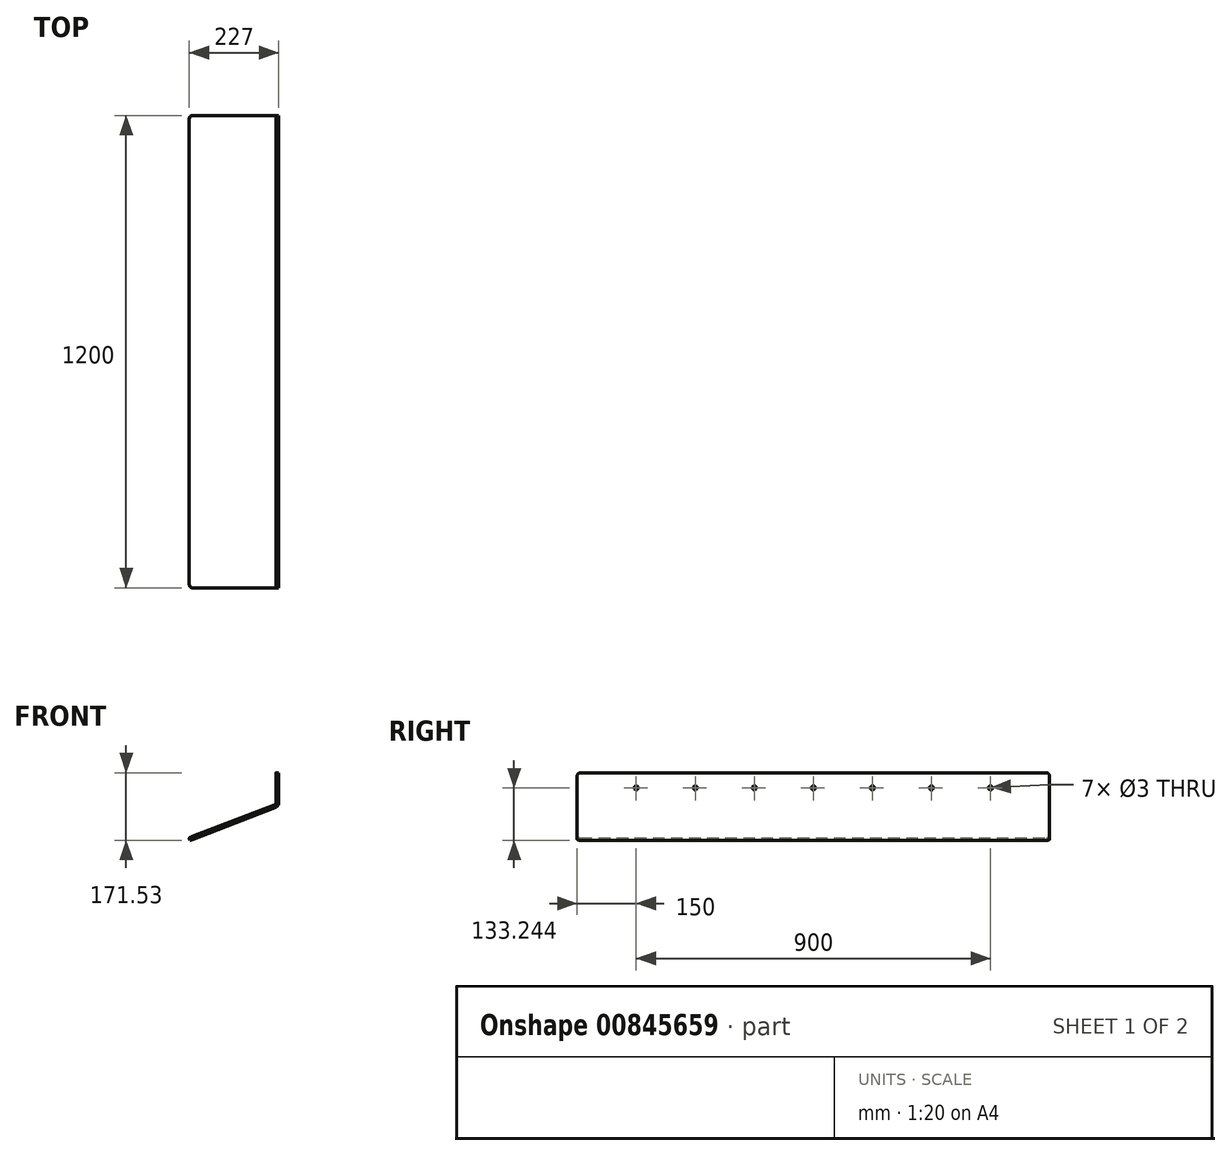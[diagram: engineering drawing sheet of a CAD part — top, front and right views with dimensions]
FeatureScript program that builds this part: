
annotation { "Feature Type Name" : "Feature", "Feature Type Description" : "" }
export const myFeature = defineFeature(function(context is Context, id is Id, definition is map)
    precondition{}
    {
        {
            var Q0;
            Q0=qCreatedBy(makeId("Front.planeOp"),FACE);
            var sketch = newSketch(context, id + "F0", { "sketchPlane" : qUnion([Q0])});
            skLineSegment(sketch, "E0", {"start": v(0, 80) * mm, "end": v(0, 3.43) * mm});
            skLineSegment(sketch, "E1", {"start": v(-3.2, -1.24) * mm, "end": v(-220, -85) * mm});
            skLineSegment(sketch, "E2", {"start": v(-220, -85) * mm, "end": v(-217.48, -91.53) * mm});
            skLineSegment(sketch, "E3", {"start": v(-217.48, -91.53) * mm, "end": v(-0.68, -7.77) * mm});
            skLineSegment(sketch, "E4", {"start": v(7, 3.43) * mm, "end": v(7, 80) * mm});
            skLineSegment(sketch, "E5", {"start": v(7, 80) * mm, "end": v(0, 80) * mm});
            skPoint(sketch, "E6.visualSharp", {"position": v(0, 0) * mm});
            skArc(sketch, "E6.filletArc", {"start": v(-3.2, -1.24) * mm, "mid": v(-0.88, 0.6) * mm, "end": v(0, 3.43) * mm});
            skPoint(sketch, "E7.visualSharp", {"position": v(7, -4.8) * mm});
            skArc(sketch, "E7.filletArc", {"start": v(-0.68, -7.77) * mm, "mid": v(4.9, -3.36) * mm, "end": v(7, 3.43) * mm});
            skSolve(sketch);
        }
        {
            var Q0;
            Q0=makeQuery(id+"F0.imprint","IMPRINT",FACE,{"disambiguationData":[TD([[makeQuery(id+"F0.imprint","IMPRINT",EDGE,{"derivedFrom":sQuery(id+"F0.wireOp",EDGE,"E0")}),1.0]])]});
            extrude(context, id + "F1", {"entities" : qUnion([Q0]), "depth" : 1200 * mm, "offsetDistance" : 25 * mm});
        }
        {
            var Q0;
            Q0=makeQuery(id+"F1.opExtrude","CAP_EDGE",EDGE,{"disambiguationData":[OSD([sQuery(id+"F0.wireOp",EDGE,"E5")])],"isStart":false});
            var Q1;
            Q1=makeQuery(id+"F1.opExtrude","CAP_EDGE",EDGE,{"disambiguationData":[OSD([sQuery(id+"F0.wireOp",EDGE,"E5")])],"isStart":true});
            var Q2;
            Q2=makeQuery(id+"F1.opExtrude","CAP_EDGE",EDGE,{"disambiguationData":[OSD([sQuery(id+"F0.wireOp",EDGE,"E2")])],"isStart":true});
            var Q3;
            Q3=makeQuery(id+"F1.opExtrude","CAP_EDGE",EDGE,{"disambiguationData":[OSD([sQuery(id+"F0.wireOp",EDGE,"E2")])],"isStart":false});
            fillet(context, id + "F2", {"entities" : qUnion([Q0, Q1, Q2, Q3]), "radius" : 8 * mm, "tangentPropagation" : true, "allowEdgeOverflow" : false});
        }
        {
            var Q0;
            Q0=makeQuery(id+"F1.opExtrude","SWEPT_FACE",FACE,{"disambiguationData":[OSD([sQuery(id+"F0.wireOp",EDGE,"E4")])]});
            var sketch = newSketch(context, id + "F3", { "sketchPlane" : qUnion([Q0])});
            skLineSegment(sketch, "E8", {"start": v(-1288.33, 41.71) * mm, "end": v(83.25, 41.71) * mm, "construction": true});
            skPoint(sketch, "E9", {"position": v(-1050, 41.71) * mm});
            skPoint(sketch, "E10", {"position": v(-900, 41.71) * mm});
            skPoint(sketch, "E11", {"position": v(-750, 41.71) * mm});
            skPoint(sketch, "E12", {"position": v(-600, 41.71) * mm});
            skPoint(sketch, "E13", {"position": v(-450, 41.71) * mm});
            skPoint(sketch, "E14", {"position": v(-300, 41.71) * mm});
            skPoint(sketch, "E15", {"position": v(-150, 41.71) * mm});
            skSolve(sketch);
        }
        {
            var Q0;
            Q0=sQuery(id+"F3.wireOp",VERTEX,"E10");
            var Q1;
            Q1=sQuery(id+"F3.wireOp",VERTEX,"E9");
            var Q2;
            Q2=sQuery(id+"F3.wireOp",VERTEX,"E11");
            var Q3;
            Q3=sQuery(id+"F3.wireOp",VERTEX,"E12");
            var Q4;
            Q4=sQuery(id+"F3.wireOp",VERTEX,"E13");
            var Q5;
            Q5=sQuery(id+"F3.wireOp",VERTEX,"E14");
            var Q6;
            Q6=sQuery(id+"F3.wireOp",VERTEX,"E15");
            var Q7;
            Q7=makeQuery(id+"F1.opExtrude","SWEPT_BODY",BODY,{"disambiguationData":[OSD([sQuery(id+"F0.wireOp",EDGE,"E0"),sQuery(id+"F0.wireOp",EDGE,"E1"),sQuery(id+"F0.wireOp",EDGE,"E2"),sQuery(id+"F0.wireOp",EDGE,"E3"),sQuery(id+"F0.wireOp",EDGE,"E4"),sQuery(id+"F0.wireOp",EDGE,"E5"),sQuery(id+"F0.wireOp",EDGE,"E6.filletArc"),sQuery(id+"F0.wireOp",EDGE,"E7.filletArc")])]});
            hole(context, id + "F4", {"style" : HoleStyle.C_SINK, "endStyle" : HoleEndStyle.THROUGH, "holeDiameter" : 3 * mm, "cSinkDiameter" : 10 * mm, "cSinkAngle" : 90 * degree, "majorDiameter" : 5 * mm, "isTappedThrough" : true, "tappedDepth" : 12 * mm, "tapClearance" : 3, "locations" : qUnion([Q0, Q1, Q2, Q3, Q4, Q5, Q6]), "scope" : qUnion([Q7])});
        }
    });
